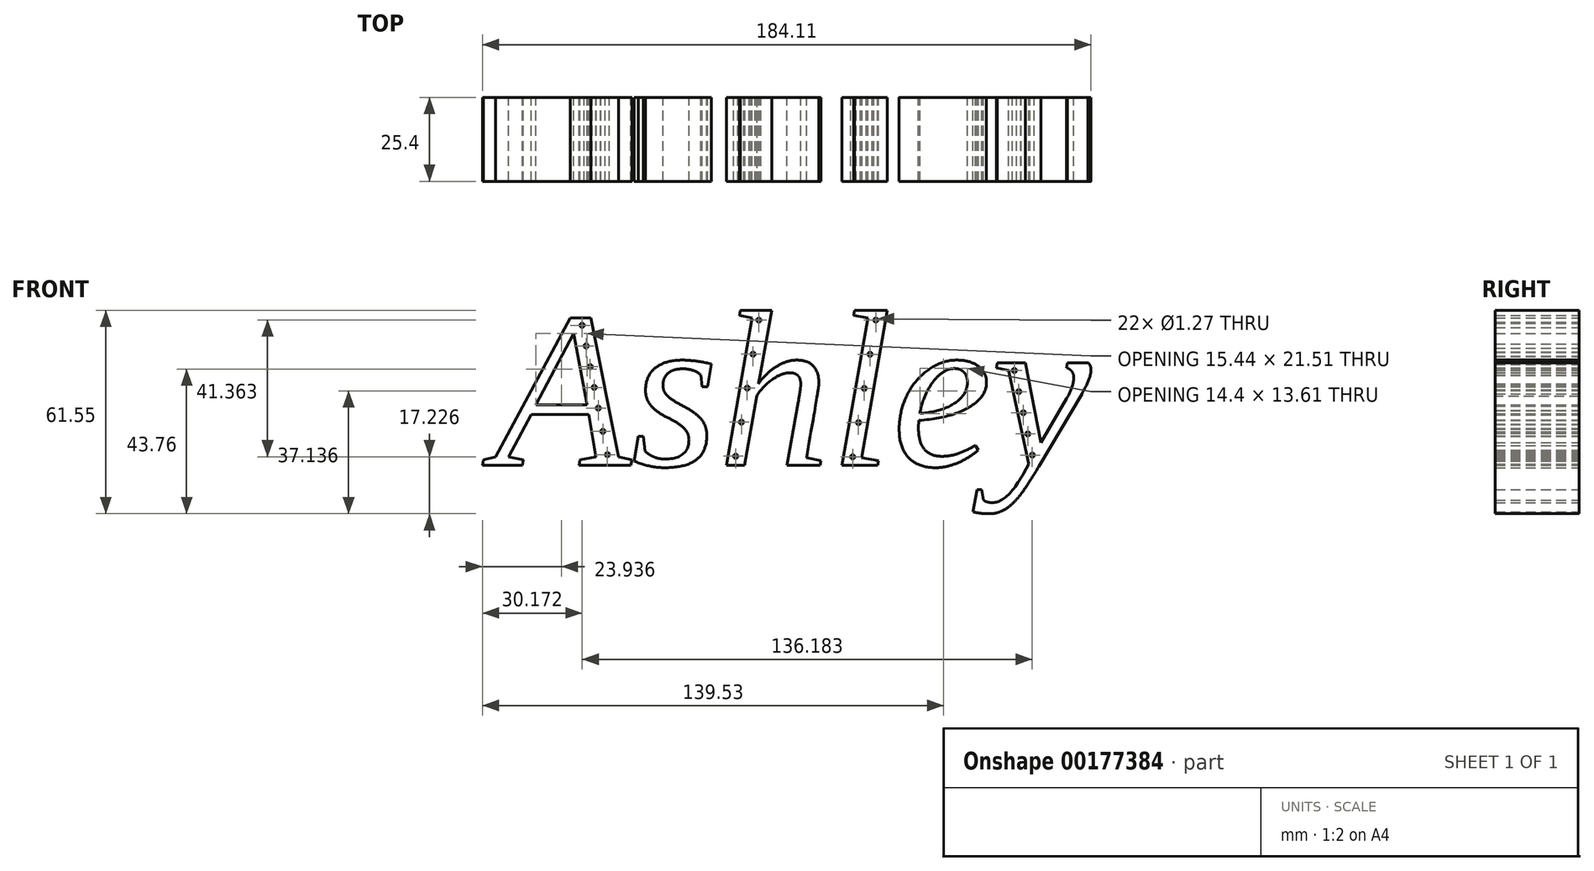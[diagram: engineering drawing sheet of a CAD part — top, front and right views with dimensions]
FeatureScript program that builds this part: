
annotation { "Feature Type Name" : "Feature", "Feature Type Description" : "" }
export const myFeature = defineFeature(function(context is Context, id is Id, definition is map)
    precondition{}
    {
        {
            var Q0;
            Q0=qCreatedBy(makeId("Front.planeOp"),FACE);
            var sketch = newSketch(context, id + "F0", { "sketchPlane" : qUnion([Q0])});
            skText(sketch, "E0", { "text": "Ashley", "fontName": "Tinos-Italic.ttf"});
            const initialGuessF0  = {"E0": [-0.0936, -0.02024, 1, 0, 0.04872]};
            skSetInitialGuess(sketch, initialGuessF0);
            skSolve(sketch);
        }
        {
            var Q0;
            Q0 = qSketchRegion(id + "F0", true);
            extrude(context, id + "F1", {"entities" : qUnion([Q0]), "depth" : 25.4 * mm});
        }
        {
            var Q0;
            Q0=qCreatedBy(makeId("Front.planeOp"),FACE);
            var sketch = newSketch(context, id + "F2", { "sketchPlane" : qUnion([Q0])});
            skPoint(sketch, "E1", {"position": v(-83.43, -2.9) * mm});
            skPoint(sketch, "E2", {"position": v(-62.22, -2.9) * mm});
            skLineSegment(sketch, "E3", {"start": v(-83.43, -2.9) * mm, "end": v(-62.22, -2.9) * mm});
            skPoint(sketch, "E4", {"position": v(-72.82, -2.9) * mm});
            skLineSegment(sketch, "E5", {"start": v(-72.82, -2.9) * mm, "end": v(-62.22, -2.9) * mm});
            skLineSegment(sketch, "E6", {"start": v(-83.43, -2.9) * mm, "end": v(-72.82, -2.9) * mm});
            skPoint(sketch, "E7", {"position": v(-78.13, -2.9) * mm});
            skPoint(sketch, "E8", {"position": v(-67.52, -2.9) * mm});
            skLineSegment(sketch, "E9", {"start": v(-62.22, -2.9) * mm, "end": v(-67.13, 22.17) * mm});
            skLineSegment(sketch, "E10", {"start": v(-67.13, 22.17) * mm, "end": v(-62.22, -2.9) * mm});
            skLineSegment(sketch, "E11", {"start": v(-62.22, -2.9) * mm, "end": v(-59.47, -16.96) * mm});
            skPoint(sketch, "E12", {"position": v(-60.84, -9.93) * mm});
            skPoint(sketch, "E13", {"position": v(-64.67, 9.64) * mm});
            skLineSegment(sketch, "E14", {"start": v(-64.67, 9.64) * mm, "end": v(-62.22, -2.9) * mm});
            skLineSegment(sketch, "E15", {"start": v(-64.67, 9.64) * mm, "end": v(-67.13, 22.17) * mm});
            skPoint(sketch, "E16", {"position": v(-65.9, 15.9) * mm});
            skPoint(sketch, "E17", {"position": v(-63.45, 3.37) * mm});
            skLineSegment(sketch, "E18", {"start": v(-13.67, 23.75) * mm, "end": v(-20.68, -17.44) * mm});
            skPoint(sketch, "E19", {"position": v(-17.18, 3.15) * mm});
            skLineSegment(sketch, "E20", {"start": v(-17.18, 3.15) * mm, "end": v(-13.67, 23.75) * mm});
            skLineSegment(sketch, "E21", {"start": v(-17.18, 3.15) * mm, "end": v(-20.68, -17.44) * mm});
            skPoint(sketch, "E22", {"position": v(-15.42, 13.45) * mm});
            skPoint(sketch, "E23", {"position": v(-18.93, -7.14) * mm});
            skLineSegment(sketch, "E24", {"start": v(21.73, 23.75) * mm, "end": v(14.72, -17.61) * mm});
            skPoint(sketch, "E25", {"position": v(18.23, 3.07) * mm});
            skLineSegment(sketch, "E26", {"start": v(18.23, 3.07) * mm, "end": v(21.73, 23.75) * mm});
            skLineSegment(sketch, "E27", {"start": v(18.23, 3.07) * mm, "end": v(14.72, -17.61) * mm});
            skPoint(sketch, "E28", {"position": v(16.48, -7.27) * mm});
            skPoint(sketch, "E29", {"position": v(19.98, 13.4) * mm});
            skLineSegment(sketch, "E30", {"start": v(63.62, 8.5) * mm, "end": v(69.06, -17.09) * mm});
            skLineSegment(sketch, "E31", {"start": v(69.06, -17.09) * mm, "end": v(66.34, -4.3) * mm});
            skLineSegment(sketch, "E32", {"start": v(66.34, -4.3) * mm, "end": v(67.7, -10.7) * mm});
            skLineSegment(sketch, "E33", {"start": v(67.7, -10.7) * mm, "end": v(66.34, -4.3) * mm});
            skLineSegment(sketch, "E34", {"start": v(63.62, 8.5) * mm, "end": v(66.34, -4.3) * mm});
            skPoint(sketch, "E35", {"position": v(64.98, 2.1) * mm});
            skPoint(sketch, "E36", {"position": v(66.34, -4.3) * mm});
            skPoint(sketch, "E37", {"position": v(67.7, -10.7) * mm});
            skPoint(sketch, "E38", {"position": v(69.06, -17.09) * mm});
            skSolve(sketch);
        }
        {
            var Q0;
            Q0=sQuery(id+"F2.wireOp",VERTEX,"E15.end");
            var Q1;
            Q1=sQuery(id+"F2.wireOp",VERTEX,"E16");
            var Q2;
            Q2=sQuery(id+"F2.wireOp",VERTEX,"E13");
            var Q3;
            Q3=sQuery(id+"F2.wireOp",VERTEX,"E17");
            var Q4;
            Q4=sQuery(id+"F2.wireOp",VERTEX,"E2");
            var Q5;
            Q5=sQuery(id+"F2.wireOp",VERTEX,"E12");
            var Q6;
            Q6=sQuery(id+"F2.wireOp",VERTEX,"E22");
            var Q7;
            Q7=sQuery(id+"F2.wireOp",VERTEX,"E18.start");
            var Q8;
            Q8=sQuery(id+"F2.wireOp",VERTEX,"E19");
            var Q9;
            Q9=sQuery(id+"F2.wireOp",VERTEX,"E23");
            var Q10;
            Q10=sQuery(id+"F2.wireOp",VERTEX,"E18.end");
            var Q11;
            Q11=sQuery(id+"F2.wireOp",VERTEX,"E29");
            var Q12;
            Q12=sQuery(id+"F2.wireOp",VERTEX,"E25");
            var Q13;
            Q13=sQuery(id+"F2.wireOp",VERTEX,"E28");
            var Q14;
            Q14=sQuery(id+"F2.wireOp",VERTEX,"E24.end");
            var Q15;
            Q15=sQuery(id+"F2.wireOp",VERTEX,"E35");
            var Q16;
            Q16=sQuery(id+"F2.wireOp",VERTEX,"E34.start");
            var Q17;
            Q17=sQuery(id+"F2.wireOp",VERTEX,"E36");
            var Q18;
            Q18=sQuery(id+"F2.wireOp",VERTEX,"E37");
            var Q19;
            Q19=sQuery(id+"F2.wireOp",VERTEX,"E38");
            var Q20;
            Q20=sQuery(id+"F2.wireOp",VERTEX,"E24.start");
            var Q21;
            Q21=sQuery(id+"F2.wireOp",VERTEX,"E11.end");
            var Q22;
            Q22=makeQuery(id+"F1.opExtrude","SWEPT_BODY",BODY,{"disambiguationData":[OSD([sQuery(id+"F0.wireOp",EDGE,"E0.sketch_text.stroke-0"),sQuery(id+"F0.wireOp",EDGE,"E0.sketch_text.stroke-1"),sQuery(id+"F0.wireOp",EDGE,"E0.sketch_text.stroke-2"),sQuery(id+"F0.wireOp",EDGE,"E0.sketch_text.stroke-3"),sQuery(id+"F0.wireOp",EDGE,"E0.sketch_text.stroke-4"),sQuery(id+"F0.wireOp",EDGE,"E0.sketch_text.stroke-5"),sQuery(id+"F0.wireOp",EDGE,"E0.sketch_text.stroke-6"),sQuery(id+"F0.wireOp",EDGE,"E0.sketch_text.stroke-7"),sQuery(id+"F0.wireOp",EDGE,"E0.sketch_text.stroke-8"),sQuery(id+"F0.wireOp",EDGE,"E0.sketch_text.stroke-9"),sQuery(id+"F0.wireOp",EDGE,"E0.sketch_text.stroke-10"),sQuery(id+"F0.wireOp",EDGE,"E0.sketch_text.stroke-11"),sQuery(id+"F0.wireOp",EDGE,"E0.sketch_text.stroke-12"),sQuery(id+"F0.wireOp",EDGE,"E0.sketch_text.stroke-13"),sQuery(id+"F0.wireOp",EDGE,"E0.sketch_text.stroke-14"),sQuery(id+"F0.wireOp",EDGE,"E0.sketch_text.stroke-15"),sQuery(id+"F0.wireOp",EDGE,"E0.sketch_text.stroke-16"),sQuery(id+"F0.wireOp",EDGE,"E0.sketch_text.stroke-17"),sQuery(id+"F0.wireOp",EDGE,"E0.sketch_text.stroke-18")])]});
            var Q23;
            Q23=makeQuery(id+"F1.opExtrude","SWEPT_BODY",BODY,{"disambiguationData":[OSD([sQuery(id+"F0.wireOp",EDGE,"E0.sketch_text.stroke-45"),sQuery(id+"F0.wireOp",EDGE,"E0.sketch_text.stroke-46"),sQuery(id+"F0.wireOp",EDGE,"E0.sketch_text.stroke-47"),sQuery(id+"F0.wireOp",EDGE,"E0.sketch_text.stroke-48"),sQuery(id+"F0.wireOp",EDGE,"E0.sketch_text.stroke-49"),sQuery(id+"F0.wireOp",EDGE,"E0.sketch_text.stroke-50"),sQuery(id+"F0.wireOp",EDGE,"E0.sketch_text.stroke-51"),sQuery(id+"F0.wireOp",EDGE,"E0.sketch_text.stroke-52"),sQuery(id+"F0.wireOp",EDGE,"E0.sketch_text.stroke-53"),sQuery(id+"F0.wireOp",EDGE,"E0.sketch_text.stroke-54"),sQuery(id+"F0.wireOp",EDGE,"E0.sketch_text.stroke-55"),sQuery(id+"F0.wireOp",EDGE,"E0.sketch_text.stroke-56"),sQuery(id+"F0.wireOp",EDGE,"E0.sketch_text.stroke-57"),sQuery(id+"F0.wireOp",EDGE,"E0.sketch_text.stroke-58"),sQuery(id+"F0.wireOp",EDGE,"E0.sketch_text.stroke-59"),sQuery(id+"F0.wireOp",EDGE,"E0.sketch_text.stroke-60"),sQuery(id+"F0.wireOp",EDGE,"E0.sketch_text.stroke-61"),sQuery(id+"F0.wireOp",EDGE,"E0.sketch_text.stroke-62"),sQuery(id+"F0.wireOp",EDGE,"E0.sketch_text.stroke-63"),sQuery(id+"F0.wireOp",EDGE,"E0.sketch_text.stroke-64"),sQuery(id+"F0.wireOp",EDGE,"E0.sketch_text.stroke-65"),sQuery(id+"F0.wireOp",EDGE,"E0.sketch_text.stroke-66"),sQuery(id+"F0.wireOp",EDGE,"E0.sketch_text.stroke-67")])]});
            var Q24;
            Q24=makeQuery(id+"F1.opExtrude","SWEPT_BODY",BODY,{"disambiguationData":[OSD([sQuery(id+"F0.wireOp",EDGE,"E0.sketch_text.stroke-68"),sQuery(id+"F0.wireOp",EDGE,"E0.sketch_text.stroke-69"),sQuery(id+"F0.wireOp",EDGE,"E0.sketch_text.stroke-70"),sQuery(id+"F0.wireOp",EDGE,"E0.sketch_text.stroke-71"),sQuery(id+"F0.wireOp",EDGE,"E0.sketch_text.stroke-72"),sQuery(id+"F0.wireOp",EDGE,"E0.sketch_text.stroke-73"),sQuery(id+"F0.wireOp",EDGE,"E0.sketch_text.stroke-74"),sQuery(id+"F0.wireOp",EDGE,"E0.sketch_text.stroke-75")])]});
            var Q25;
            Q25=makeQuery(id+"F1.opExtrude","SWEPT_BODY",BODY,{"disambiguationData":[OSD([sQuery(id+"F0.wireOp",EDGE,"E0.sketch_text.stroke-100"),sQuery(id+"F0.wireOp",EDGE,"E0.sketch_text.stroke-101"),sQuery(id+"F0.wireOp",EDGE,"E0.sketch_text.stroke-102"),sQuery(id+"F0.wireOp",EDGE,"E0.sketch_text.stroke-103"),sQuery(id+"F0.wireOp",EDGE,"E0.sketch_text.stroke-104"),sQuery(id+"F0.wireOp",EDGE,"E0.sketch_text.stroke-105"),sQuery(id+"F0.wireOp",EDGE,"E0.sketch_text.stroke-106"),sQuery(id+"F0.wireOp",EDGE,"E0.sketch_text.stroke-107"),sQuery(id+"F0.wireOp",EDGE,"E0.sketch_text.stroke-108"),sQuery(id+"F0.wireOp",EDGE,"E0.sketch_text.stroke-109"),sQuery(id+"F0.wireOp",EDGE,"E0.sketch_text.stroke-110"),sQuery(id+"F0.wireOp",EDGE,"E0.sketch_text.stroke-111"),sQuery(id+"F0.wireOp",EDGE,"E0.sketch_text.stroke-112"),sQuery(id+"F0.wireOp",EDGE,"E0.sketch_text.stroke-113"),sQuery(id+"F0.wireOp",EDGE,"E0.sketch_text.stroke-114"),sQuery(id+"F0.wireOp",EDGE,"E0.sketch_text.stroke-115"),sQuery(id+"F0.wireOp",EDGE,"E0.sketch_text.stroke-116"),sQuery(id+"F0.wireOp",EDGE,"E0.sketch_text.stroke-117"),sQuery(id+"F0.wireOp",EDGE,"E0.sketch_text.stroke-118"),sQuery(id+"F0.wireOp",EDGE,"E0.sketch_text.stroke-119"),sQuery(id+"F0.wireOp",EDGE,"E0.sketch_text.stroke-120"),sQuery(id+"F0.wireOp",EDGE,"E0.sketch_text.stroke-121"),sQuery(id+"F0.wireOp",EDGE,"E0.sketch_text.stroke-122"),sQuery(id+"F0.wireOp",EDGE,"E0.sketch_text.stroke-123")])]});
            hole(context, id + "F3", {"style" : HoleStyle.SIMPLE, "endStyle" : HoleEndStyle.THROUGH, "oppositeDirection" : true, "holeDiameter" : 1.27 * mm, "locations" : qUnion([Q0, Q1, Q2, Q3, Q4, Q5, Q6, Q7, Q8, Q9, Q10, Q11, Q12, Q13, Q14, Q15, Q16, Q17, Q18, Q19, Q20, Q21]), "scope" : qUnion([Q22, Q23, Q24, Q25]), "isTappedThrough" : true});
        }
    });
